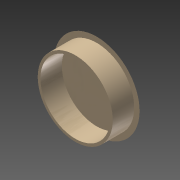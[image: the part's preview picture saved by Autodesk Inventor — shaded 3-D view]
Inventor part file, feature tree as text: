
AUTODESK INVENTOR PART (.ipt)
format: ipt  version: 2015 (Build 190159000, 159)  size: 115,712 bytes
history: native  units: mm
features: sketch x2, other x1, extrude x1, shell x1, revolve x1
ambient origin geometry x8: Origin, YZ Plane, XZ Plane, XY Plane, X Axis, Y Axis, Z Axis, Center Point
bodies: Body1 (feature_tree)
feature tree (6):
  other  "Bryła1"
  extrude  "Wyciągnięcie proste1"  Depth=28.0mm
  shell  "Skorupa1"  Thickness=8.0mm
  revolve  "Obrót1"
  sketch  "Szkic1"
  sketch  "Szkic2"
